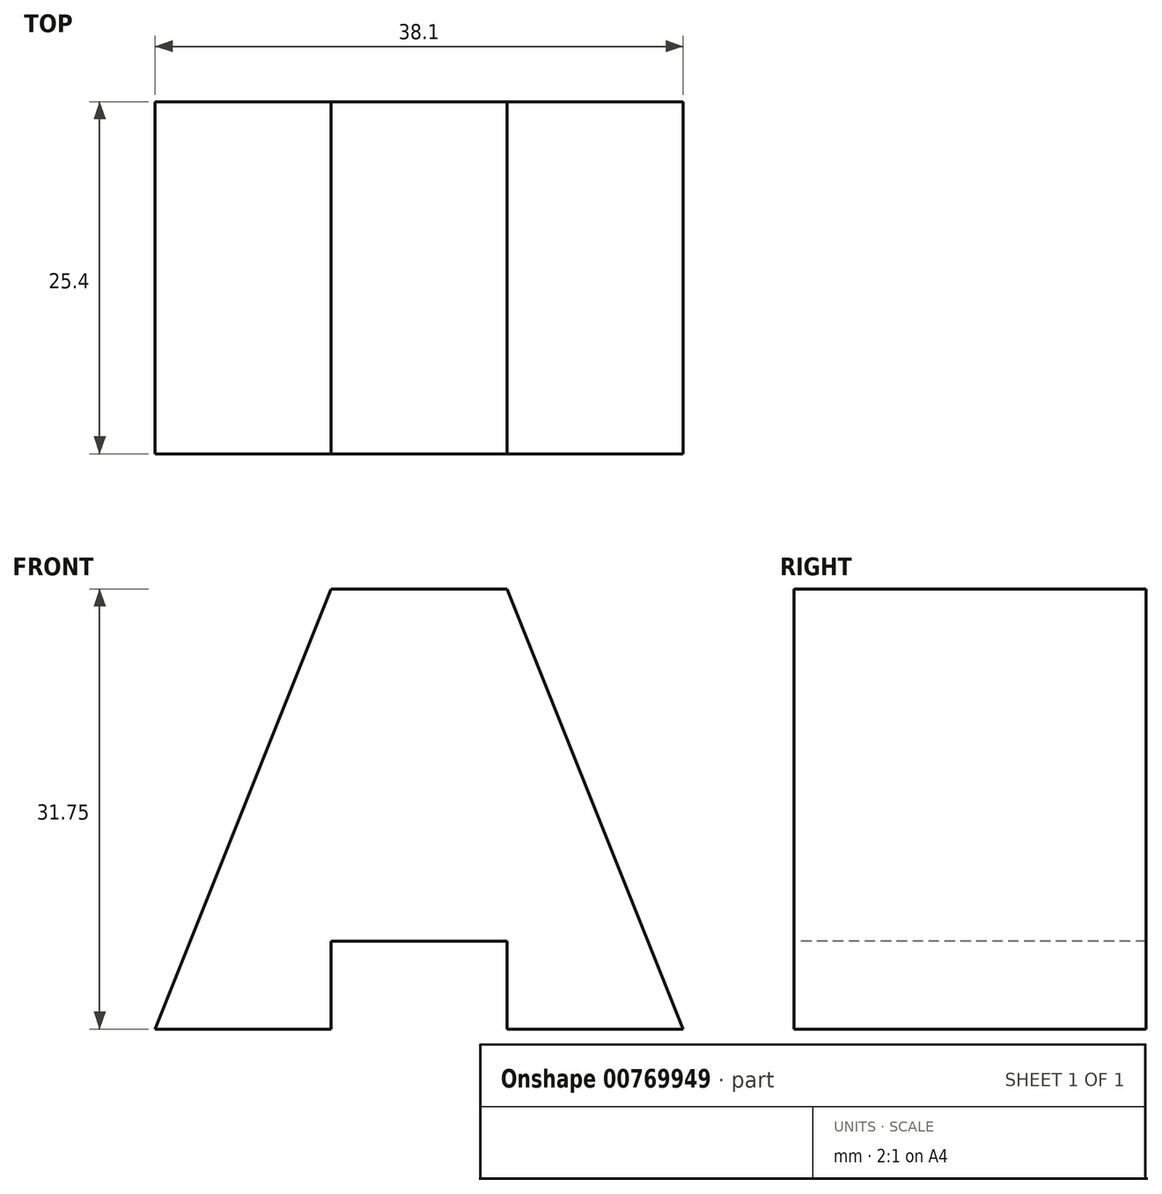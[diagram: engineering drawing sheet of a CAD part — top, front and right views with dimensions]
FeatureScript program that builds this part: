
annotation { "Feature Type Name" : "Feature", "Feature Type Description" : "" }
export const myFeature = defineFeature(function(context is Context, id is Id, definition is map)
    precondition{}
    {
        {
            var Q0;
            Q0=qCreatedBy(makeId("Front.planeOp"),FACE);
            var sketch = newSketch(context, id + "F0", { "sketchPlane" : qUnion([Q0])});
            skLineSegment(sketch, "E0", {"start": v(0, 0) * mm, "end": v(38.1, 0) * mm});
            skLineSegment(sketch, "E1", {"start": v(38.1, 0) * mm, "end": v(38.1, 31.75) * mm});
            skLineSegment(sketch, "E2", {"start": v(38.1, 31.75) * mm, "end": v(0, 31.75) * mm});
            skLineSegment(sketch, "E3", {"start": v(0, 31.75) * mm, "end": v(0, 0) * mm});
            skSolve(sketch);
        }
        {
            var Q0;
            Q0=makeQuery(id+"F0.imprint","IMPRINT",FACE,{"disambiguationData":[TD([[makeQuery(id+"F0.imprint","IMPRINT",EDGE,{"derivedFrom":sQuery(id+"F0.wireOp",EDGE,"E0")}),1.0]])]});
            extrude(context, id + "F1", {"entities" : qUnion([Q0]), "depth" : 25.4 * mm, "offsetDistance" : 25.4 * mm});
        }
        {
            var Q0;
            Q0=makeQuery(id+"F1.opExtrude","CAP_FACE",FACE,{"disambiguationData":[OSD([sQuery(id+"F0.wireOp",EDGE,"E0"),sQuery(id+"F0.wireOp",EDGE,"E1"),sQuery(id+"F0.wireOp",EDGE,"E2"),sQuery(id+"F0.wireOp",EDGE,"E3")])],"isStart":false});
            var sketch = newSketch(context, id + "F2", { "sketchPlane" : qUnion([Q0])});
            skLineSegment(sketch, "E4", {"start": v(0, 0) * mm, "end": v(12.7, 0) * mm});
            skLineSegment(sketch, "E5", {"start": v(38.1, 0) * mm, "end": v(25.4, 0) * mm});
            skLineSegment(sketch, "E6", {"start": v(25.4, 0) * mm, "end": v(25.4, 6.35) * mm});
            skLineSegment(sketch, "E7", {"start": v(25.4, 6.35) * mm, "end": v(12.7, 6.35) * mm});
            skLineSegment(sketch, "E8", {"start": v(12.7, 6.35) * mm, "end": v(12.7, 0) * mm});
            skSolve(sketch);
        }
        {
            var Q0;
            {var subQ0=sQuery(id+"F2.wireOp",EDGE,"E6");Q0=makeQuery(id+"F2.imprint","IMPRINT",FACE,{"disambiguationData":[TD([[makeQuery(id+"F2.imprint","IMPRINT",EDGE,{"derivedFrom":subQ0}),1.0]])]});}
            extrude(context, id + "F3", {"entities" : qUnion([Q0]), "operationType" : NewBodyOperationType.REMOVE, "oppositeDirection" : true, "depth" : 25.4 * mm, "offsetDistance" : 25.4 * mm});
        }
        {
            var Q0;
            Q0=makeQuery(id+"F1.opExtrude","CAP_FACE",FACE,{"disambiguationData":[OSD([sQuery(id+"F0.wireOp",EDGE,"E0"),sQuery(id+"F0.wireOp",EDGE,"E1"),sQuery(id+"F0.wireOp",EDGE,"E2"),sQuery(id+"F0.wireOp",EDGE,"E3")])],"isStart":false});
            var sketch = newSketch(context, id + "F4", { "sketchPlane" : qUnion([Q0])});
            skLineSegment(sketch, "E9", {"start": v(38.1, 31.75) * mm, "end": v(25.4, 31.75) * mm});
            skLineSegment(sketch, "E10", {"start": v(0, 31.75) * mm, "end": v(12.7, 31.75) * mm});
            skLineSegment(sketch, "E11", {"start": v(0, 0) * mm, "end": v(12.7, 31.75) * mm});
            skLineSegment(sketch, "E12", {"start": v(25.4, 31.75) * mm, "end": v(38.1, 0) * mm});
            skLineSegment(sketch, "E13", {"start": v(38.1, 0) * mm, "end": v(25.4, 31.75) * mm});
            skLineSegment(sketch, "E14", {"start": v(25.4, 31.75) * mm, "end": v(12.7, 31.75) * mm});
            skSolve(sketch);
        }
        {
            var Q0;
            Q0=makeQuery(id+"F4.imprint","IMPRINT",FACE,{"disambiguationData":[TD([[makeQuery(id+"F4.imprint","IMPRINT",EDGE,{"derivedFrom":sQuery(id+"F4.wireOp",EDGE,"E9")}),1.0]])]});
            extrude(context, id + "F5", {"entities" : qUnion([Q0]), "operationType" : NewBodyOperationType.REMOVE, "oppositeDirection" : true, "depth" : 25.4 * mm, "offsetDistance" : 25.4 * mm});
        }
        {
            var Q0;
            Q0=makeQuery(id+"F1.opExtrude","CAP_FACE",FACE,{"disambiguationData":[OSD([sQuery(id+"F0.wireOp",EDGE,"E0"),sQuery(id+"F0.wireOp",EDGE,"E1"),sQuery(id+"F0.wireOp",EDGE,"E2"),sQuery(id+"F0.wireOp",EDGE,"E3")])],"isStart":false});
            var sketch = newSketch(context, id + "F6", { "sketchPlane" : qUnion([Q0])});
            skLineSegment(sketch, "E15", {"start": v(25.4, 31.75) * mm, "end": v(12.7, 31.75) * mm});
            skLineSegment(sketch, "E16", {"start": v(12.7, 31.75) * mm, "end": v(0, 0) * mm});
            skLineSegment(sketch, "E17", {"start": v(0, 0) * mm, "end": v(0, 31.75) * mm});
            skLineSegment(sketch, "E18", {"start": v(0, 31.75) * mm, "end": v(12.7, 31.75) * mm});
            skSolve(sketch);
        }
        {
            var Q0;
            Q0=makeQuery(id+"F6.imprint","IMPRINT",FACE,{"disambiguationData":[TD([[makeQuery(id+"F6.imprint","IMPRINT",EDGE,{"derivedFrom":sQuery(id+"F6.wireOp",EDGE,"E16")}),-1.0]])]});
            extrude(context, id + "F7", {"entities" : qUnion([Q0]), "operationType" : NewBodyOperationType.REMOVE, "oppositeDirection" : true, "depth" : 25.4 * mm, "offsetDistance" : 25.4 * mm});
        }
    });
